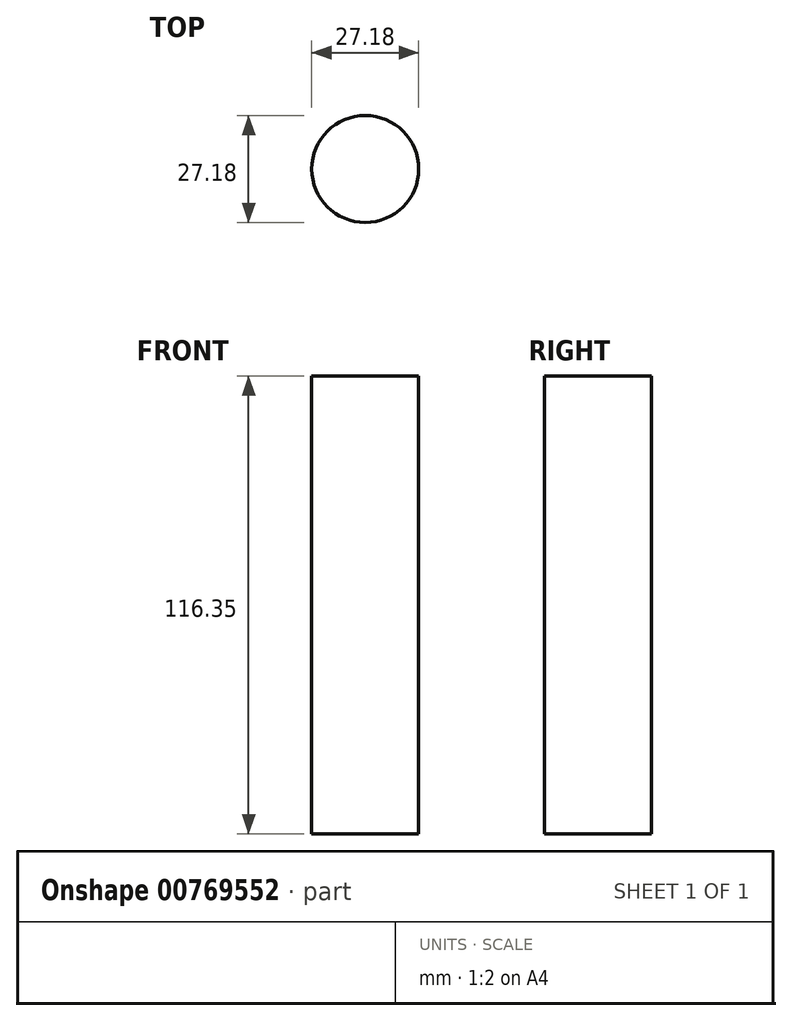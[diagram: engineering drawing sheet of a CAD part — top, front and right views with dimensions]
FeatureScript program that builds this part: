
annotation { "Feature Type Name" : "Feature", "Feature Type Description" : "" }
export const myFeature = defineFeature(function(context is Context, id is Id, definition is map)
    precondition{}
    {
        {
            var Q0;
            Q0=qCreatedBy(makeId("Front.planeOp"),FACE);
            var sketch = newSketch(context, id + "F0", { "sketchPlane" : qUnion([Q0])});
            skLineSegment(sketch, "E0.bottom", {"start": v(-13.59, 46.57) * mm, "end": v(0, 46.57) * mm});
            skLineSegment(sketch, "E0.top", {"start": v(-13.59, -69.78) * mm, "end": v(0, -69.78) * mm});
            skLineSegment(sketch, "E0.left", {"start": v(-13.59, 46.57) * mm, "end": v(-13.59, -69.78) * mm});
            skLineSegment(sketch, "E0.right", {"start": v(0, 46.57) * mm, "end": v(0, -69.78) * mm});
            skLineSegment(sketch, "E1", {"start": v(0, 75.89) * mm, "end": v(0, -75.89) * mm});
            skSolve(sketch);
        }
        {
            var Q0;
            {var subQ0=sQuery(id+"F0.wireOp",EDGE,"E0.bottom");Q0=makeQuery(id+"F0.imprint","IMPRINT",FACE,{"disambiguationData":[TD([[makeQuery(id+"F0.imprint","IMPRINT",EDGE,{"derivedFrom":subQ0}),-1.0]])]});}
            var Q1;
            Q1=sQuery(id+"F0.wireOp",EDGE,"E1");
            revolve(context, id + "F1", {"surfaceOperationType" : NewSurfaceOperationType.NEW, "entities" : qUnion([Q0]), "axis" : qUnion([Q1]), "revolveType" : RevolveType.FULL});
        }
    });
